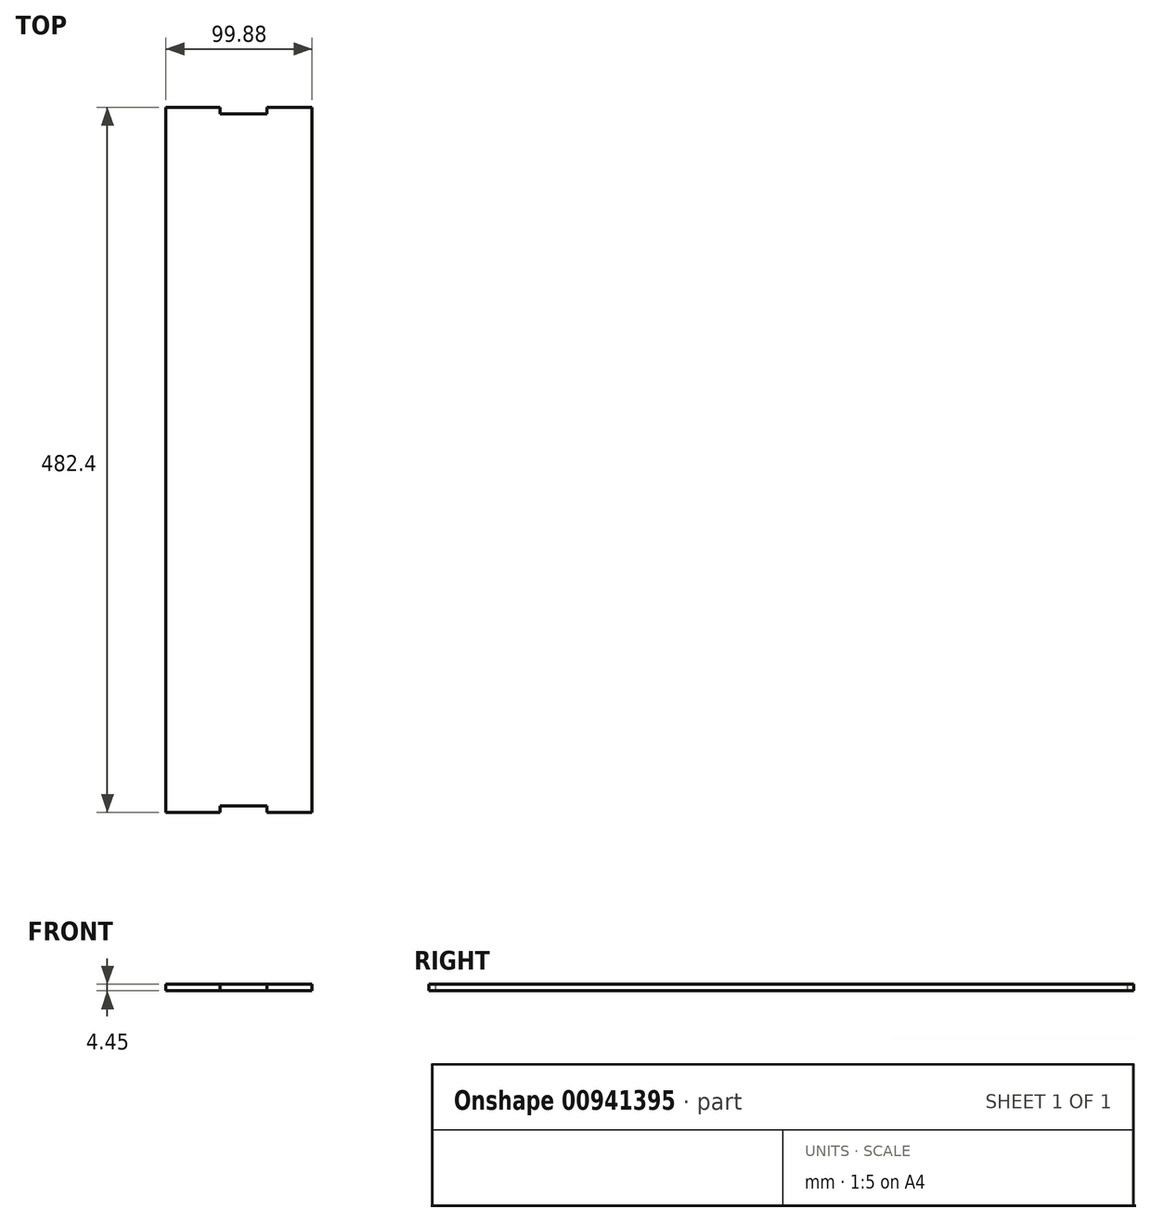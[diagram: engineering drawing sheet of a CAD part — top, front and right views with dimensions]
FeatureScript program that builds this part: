
annotation { "Feature Type Name" : "Feature", "Feature Type Description" : "" }
export const myFeature = defineFeature(function(context is Context, id is Id, definition is map)
    precondition{}
    {
        {
            var Q0;
            Q0=qCreatedBy(makeId("Top.planeOp"),FACE);
            var sketch = newSketch(context, id + "F0", { "sketchPlane" : qUnion([Q0])});
            skLineSegment(sketch, "E0.trimOffspring", {"start": v(12.26, 426.26) * mm, "end": v(12.26, 430.7) * mm});
            skLineSegment(sketch, "E1.trimOffspring", {"start": v(-56.07, 426.26) * mm, "end": v(-57, 426.26) * mm});
            skLineSegment(sketch, "E2", {"start": v(-19.85, 426.26) * mm, "end": v(-19.85, 430.7) * mm});
            skLineSegment(sketch, "E3.bottom", {"start": v(-57, 426.26) * mm, "end": v(-56.07, 426.26) * mm});
            skLineSegment(sketch, "E3.top", {"start": v(-19.85, -47.24) * mm, "end": v(12.26, -47.24) * mm});
            skLineSegment(sketch, "E3.left", {"start": v(-57, 426.26) * mm, "end": v(-57, -47.24) * mm});
            skLineSegment(sketch, "E3.right", {"start": v(42.88, 426.26) * mm, "end": v(42.88, -47.24) * mm});
            skLineSegment(sketch, "E4.bottom", {"start": v(-19.85, 430.7) * mm, "end": v(-56.07, 430.7) * mm});
            skLineSegment(sketch, "E4.left", {"start": v(-19.85, 430.7) * mm, "end": v(-19.85, 426.26) * mm});
            skLineSegment(sketch, "E5.bottom", {"start": v(12.26, 430.7) * mm, "end": v(42.88, 430.7) * mm});
            skLineSegment(sketch, "E5.left", {"start": v(12.26, 430.7) * mm, "end": v(12.26, 426.26) * mm});
            skLineSegment(sketch, "E5.right", {"start": v(42.88, 430.7) * mm, "end": v(42.88, 426.26) * mm});
            skLineSegment(sketch, "E6.bottom", {"start": v(-56.07, 430.7) * mm, "end": v(-57, 430.7) * mm});
            skLineSegment(sketch, "E6.right", {"start": v(-57, 430.7) * mm, "end": v(-57, 426.26) * mm});
            skLineSegment(sketch, "E7.trimOffspring", {"start": v(-19.85, 426.26) * mm, "end": v(12.26, 426.26) * mm});
            skLineSegment(sketch, "E8.top", {"start": v(-57, -51.7) * mm, "end": v(-19.85, -51.7) * mm});
            skLineSegment(sketch, "E8.left", {"start": v(-57, -47.24) * mm, "end": v(-57, -51.7) * mm});
            skLineSegment(sketch, "E8.right", {"start": v(-19.85, -47.24) * mm, "end": v(-19.85, -51.7) * mm});
            skLineSegment(sketch, "E9.top", {"start": v(42.88, -51.7) * mm, "end": v(12.26, -51.7) * mm});
            skLineSegment(sketch, "E9.left", {"start": v(42.88, -47.24) * mm, "end": v(42.88, -51.7) * mm});
            skLineSegment(sketch, "E9.right", {"start": v(12.26, -47.24) * mm, "end": v(12.26, -51.7) * mm});
            skSolve(sketch);
        }
        {
            var Q0;
            Q0 = qSketchRegion(id + "F0", true);
            extrude(context, id + "F1", {"entities" : qUnion([Q0]), "depth" : 4.45 * mm, "offsetDistance" : 25 * mm});
        }
    });
